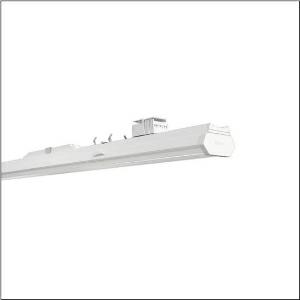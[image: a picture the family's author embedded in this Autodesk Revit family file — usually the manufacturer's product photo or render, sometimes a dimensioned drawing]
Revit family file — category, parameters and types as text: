
# Revit family: licross_21_protected_mo_52td12cn49xg
name_source: partatom
category: Lighting Fixtures
units: mm (PartAtom-declared; Revit-internal decimal feet)

## family parameters
Cut with Voids When Loaded = No
Host = Face
Light Source = No
Part Type = Normal
Room Calculation Point = No
Round Connector Dimension = Use Diameter
Shared = No

## types (1)
- --- (1 x LED, 9110 lm, 50.4 W, 4000K)
    Apparent Load = 50 VA
    CIE Flux Codes = 73 92 98 99 100
    Color Rendering = 80
    Color Temperature = 4000K
    Default Elevation = 1800 mm
    Description = Licross 21 Protected MO, luminaire insert, of sheet steel, galvanised, coil coated, white, length: 1.500mm, width: 90mm, height: 103mm, LED rated luminous flux: 9.120lm, light colour: 840, SDCM (Standard Deviation of Colour Matching)MacAdam ≤ 3 SDCM (initial), control gear: ON/OFF Multilumen, CLOi, with plug, 3-pole, with phase selection, mains connection: 220..240V, AC, 50/60Hz, start of lifetime: 50W, end of service life: 61W, internal wiring halogen-free, primary light control with lens, of plastic, primary optical cover: cover, of PMMA, light emission: direct distribution, primary light characteristic: symmetric, protection rating (complete): IP54, insulation class (complete): insulation class I (protective earthing), certification: CE, ENEC, VDE, UKCA, protection symbol: D if used in an environment with non-conductive dust loads with corresponding accessories, impact resistance: IK06, permissible ambient temperature for indoor applications: -35..+45°C, corresponds to IFS (International Featured Standards) requirements for safety and quality in the food industry, reducing of maximum allowable ambient temperature of 5°C with ceiling mounting, LABS conformity tested according to VDMA 24364:2018-05, The light source and the operating device comply with the requirements of the Ecodesign Regulation (EU) 2019/2020 and are replaceable in accordance with this regulation, packaging unit: 1 piece
    Height = 92 mm
    Lamp = 1 x LED
    Lamp Light Flux = 9110 lm
    Lamp Power = 50.4 W
    Lamp count = 1
    Length = 1500 mm
    Luminous efficacy = 181 lm/W
    Manufacturer = Siteco
    ModVariant = No
    Model = 52TD12CN49XG
    Mounting Place = Ceiling
    Mounting Type = Pendant
    Number of Poles = 1
    OnlyDefault = Yes
    Power Factor = 1
    Product Name = Licross 21 Protected MO
    Product group = luminaire insert | ceiling pendant
    ProductGroupID = 901
    Protection Class = Protection class I
    Protection Degree = IP 54
    RLX_Detail_Level = 1
    RLX_Emergency_Light_Flux = 0 lm
    RLX_Emergency_Type = 0
    RLX_Emergency_Type_DB = No
    RlxData = <blob elided: 22541 chars, md5=05045edb>
    Socket = socket
    Standby Power = 0 W
    System Light Flux = 9110 lm
    System Power = 50 W
    Type Comments = factory setting: luminous flux: 100 % | (A | C | E) | 117 mA
    Type Image = l_1256148.jpg
    URL = http://relux.com
    VarID = @adj_111153
    Voltage = 0 V
    Weight = 0.00 kg
    Width = 88 mm

## geometry (parser evidence)
native form markers: Blend x4, Sweep x12
no freeform markers — native parametric forms only
